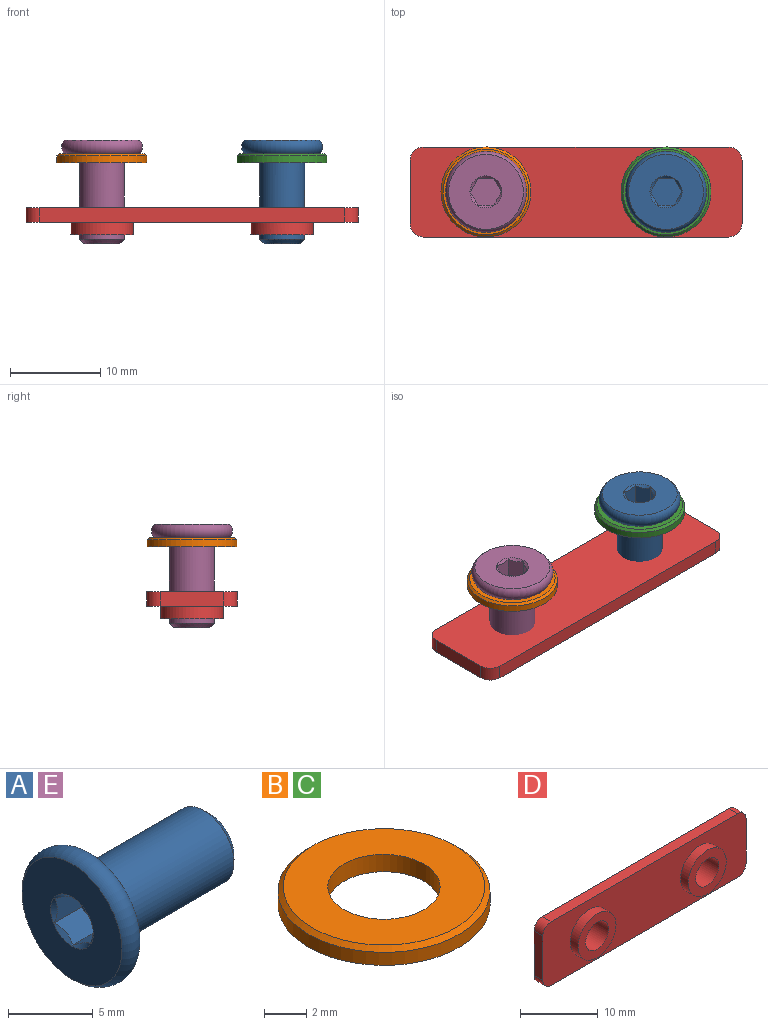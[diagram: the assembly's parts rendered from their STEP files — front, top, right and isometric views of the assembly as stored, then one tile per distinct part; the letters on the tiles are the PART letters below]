
ASSEMBLY  parts=5 mates=4
PART A: 14 faces, bbox 11.8x9.7x9.7 mm
  f0: cone r=1.78mm half-angle=45deg, axis (-1,0,0), area 3.1mm2, adj f5,f8,f9,f10,f11,f12,f13
  f1: torus R=3.5mm, axis (1,0,0), area 46.7mm2, adj f5,f6
  f2: cone r=2mm half-angle=45deg, axis (-1,0,0), area 10mm2, adj f3,f4
  f3: cylinder r=2.5mm len=9.5mm, axis (1,0,0), area 149.2mm2, adj f2,f6
  f4: plane 4x4mm, normal (1,0,0), area 12.6mm2, adj f2
  f5: plane 8.32x8.32mm, normal (-1,0,0), area 44.4mm2, adj f0,f1
  f6: plane 8.32x8.32mm, normal (1,0,0), area 34.8mm2, adj f1,f3
  f7: plane 3.46x3mm, normal (-1,0,0), area 7.8mm2, adj f8,f9,f10,f11,f12,f13
  f8: plane 2.25x1.5mm, normal (0,-0.5,-0.87), area 3.6mm2, adj f0,f7,f9,f13
  f9: plane 2.25x1.73mm, normal (0,-1,0), area 3.6mm2, adj f0,f7,f8,f10
  f10: plane 2.25x1.5mm, normal (0,-0.5,0.87), area 3.6mm2, adj f0,f7,f9,f11
  f11: plane 2.25x1.5mm, normal (0,0.5,0.87), area 3.6mm2, adj f0,f7,f10,f12
  f12: plane 2.25x1.73mm, normal (0,1,0), area 3.6mm2, adj f0,f7,f11,f13
  f13: plane 2.25x1.5mm, normal (0,0.5,-0.87), area 3.6mm2, adj f0,f7,f8,f12
PART B: 5 faces, bbox 10x10x1 mm
  f0: plane 9.5x9.5mm, normal (0,0,1), area 48.8mm2, adj f1,f4
  f1: cylinder r=2.65mm len=5.3mm, axis (0,0,-1), area 16.7mm2, adj f0,f2
  f2: plane 10x10mm, normal (0,0,-1), area 56.5mm2, adj f1,f3
  f3: cylinder r=5mm len=10mm, axis (0,0,-1), area 23.6mm2, adj f2,f4
  f4: cone r=5mm half-angle=45deg, axis (0,0,-1), area 10.8mm2, adj f0,f3
PART C: same geometry as B
PART D: 16 faces, bbox 36.9x3x10 mm
  f0: cylinder r=2.1mm len=4.2mm, axis (0,-1,0), area 39.6mm2, adj f13,f14
  f1: cylinder r=2.1mm len=4.2mm, axis (0,-1,0), area 39.6mm2, adj f13,f15
  f2: cylinder r=3.45mm len=6.9mm, axis (0,1,0), area 30.3mm2, adj f4,f15
  f3: cylinder r=3.45mm len=6.9mm, axis (0,1,0), area 30.3mm2, adj f4,f14
  f4: plane 36.88x10mm, normal (0,-1,0), area 292.1mm2, adj f2,f3,f5,f6,f7,f8,f9,f10
  f5: cylinder r=1.5mm len=1.6mm, axis (0,1,0), area 3.8mm2, adj f4,f6,f12,f13
  f6: plane 33.88x1.6mm, normal (0,0,1), area 54.2mm2, adj f4,f5,f7,f13
  f7: cylinder r=1.5mm len=1.6mm, axis (0,1,0), area 3.8mm2, adj f4,f6,f8,f13
  f8: plane 7x1.6mm, normal (-1,0,0), area 11.2mm2, adj f4,f7,f9,f13
  f9: cylinder r=1.5mm len=1.6mm, axis (0,1,0), area 3.8mm2, adj f4,f8,f10,f13
  f10: plane 33.88x1.6mm, normal (0,0,-1), area 54.2mm2, adj f4,f9,f11,f13
  f11: cylinder r=1.5mm len=1.6mm, axis (0,1,0), area 3.8mm2, adj f4,f10,f12,f13
  f12: plane 7x1.6mm, normal (1,0,0), area 11.2mm2, adj f4,f5,f11,f13
  f13: plane 36.88x10mm, normal (0,1,0), area 339.2mm2, adj f0,f1,f5,f6,f7,f8,f9,f10
  f14: plane 6.9x6.9mm, normal (0,-1,0), area 23.5mm2, adj f0,f3
  f15: plane 6.9x6.9mm, normal (0,-1,0), area 23.5mm2, adj f1,f2
PART E: same geometry as A
PLACE A rot(axis=(0,1,0),90deg) t=(10,0,-2)mm
PLACE B t=(-10,0,5.5)mm
PLACE C t=(10,0,5.5)mm
PLACE D rot(axis=(0,0.71,0.71),180deg) t=(18.44,-5,0)mm
PLACE E rot(axis=(0,1,0),90deg) t=(-10,0,-2)mm
MATE fastened E.f0 <-> B.f1  axis (0,0,-1) through (-10,0,6)mm
MATE fastened C.f1 <-> D.f0  axis (0,0,1) through (10,0,5)mm
MATE fastened B.f1 <-> D.f1  axis (0,0,1) through (-10,0,5)mm
MATE fastened A.f0 <-> C.f1  axis (0,0,-1) through (10,0,6)mm
